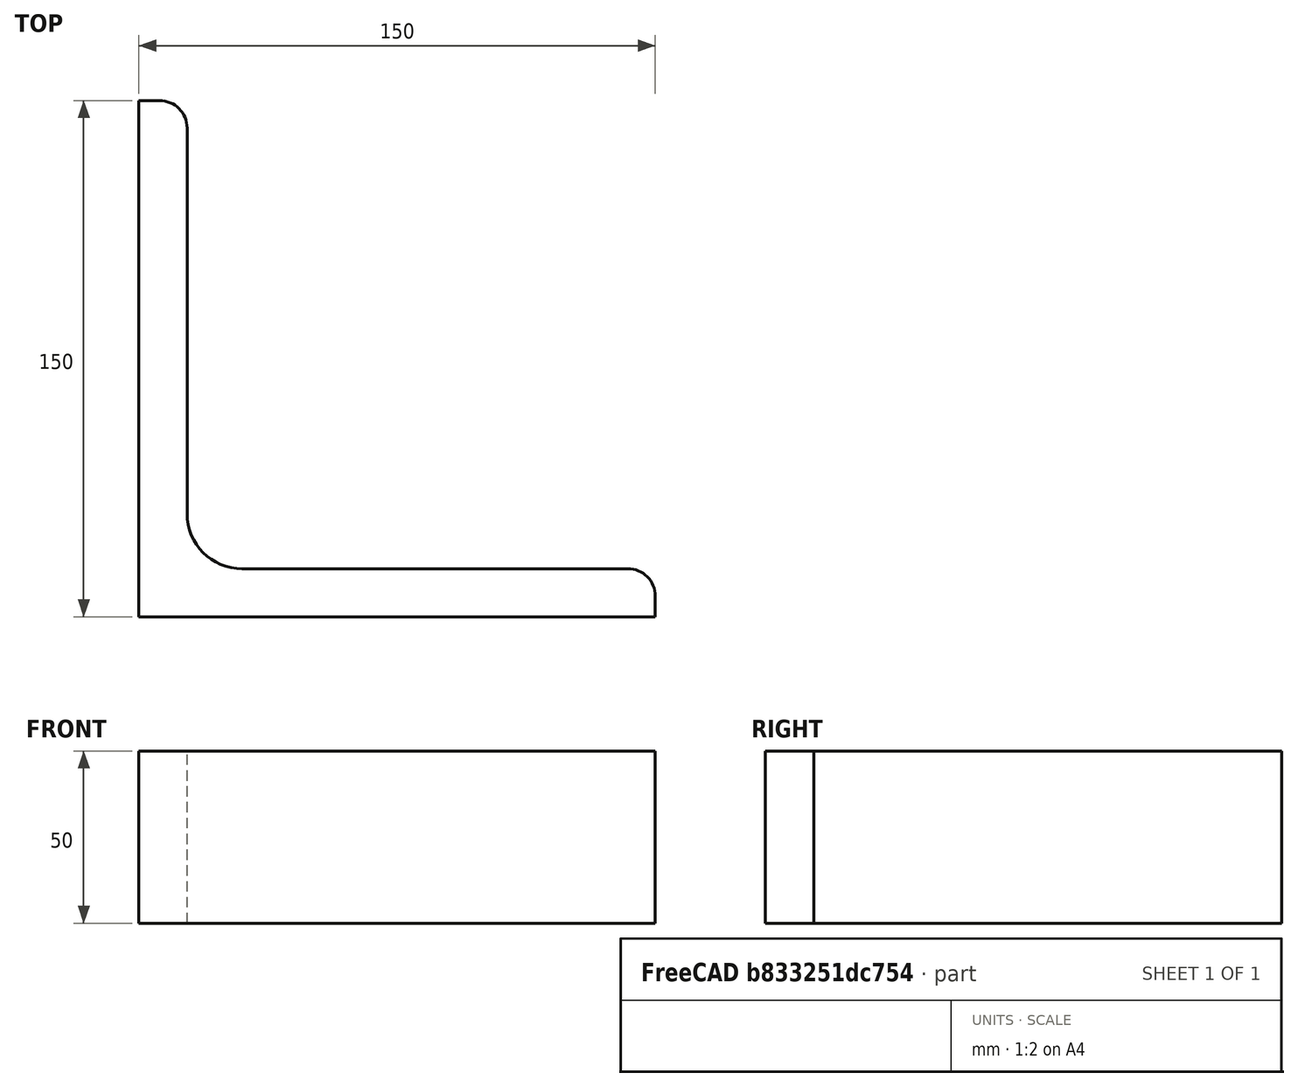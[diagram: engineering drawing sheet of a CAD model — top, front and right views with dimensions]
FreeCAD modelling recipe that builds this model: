
FCSTD DOCUMENT  (FreeCAD 0.15R4671 (Git))
Label: Angle Bar L150x150x14 EN10056 S235JR
License: All rights reserved
LicenseURL: http://en.wikipedia.org/wiki/All_rights_reserved
objects: Sketcher::SketchObject×1, Part::Extrusion×1
note: 2 computed .brp shape members not serialized (recipe doc carries the construction recipe); baked Part::Feature solids carry a one-line shape summary decoded from their .brp

FEATURE [Sketcher::SketchObject] Sketch
  sketch-geometry (9):
    g0: LineSegment StartX=0 StartY=0 StartZ=0 EndX=150 EndY=0 EndZ=0
    g1: LineSegment StartX=150 StartY=0 StartZ=0 EndX=150 EndY=6 EndZ=0
    g2: LineSegment StartX=142 StartY=14 StartZ=0 EndX=30 EndY=14 EndZ=0
    g3: LineSegment StartX=0 StartY=0 StartZ=0 EndX=0 EndY=150 EndZ=0
    g4: LineSegment StartX=0 StartY=150 StartZ=0 EndX=6 EndY=150 EndZ=0
    g5: LineSegment StartX=14 StartY=142 StartZ=0 EndX=14 EndY=30 EndZ=0
    g6: ArcOfCircle CenterX=30 CenterY=30 CenterZ=0 NormalX=0 NormalY=0 NormalZ=1 Radius=16 StartAngle=3.14159 EndAngle=4.71239
    g7: ArcOfCircle CenterX=6 CenterY=142 CenterZ=0 NormalX=0 NormalY=0 NormalZ=1 Radius=8 StartAngle=0 EndAngle=1.5708
    g8: ArcOfCircle CenterX=142 CenterY=6 CenterZ=0 NormalX=0 NormalY=0 NormalZ=1 Radius=8 StartAngle=0 EndAngle=1.5708
  constraints (23):
    c: Coincident(g0,g-1)
    c: Horizontal(g0)
    c: Coincident(g1,g0)
    c: Vertical(g1)
    c: Horizontal(g2)
    c: Coincident(g3,g-1)
    c: Vertical(g3)
    c: Coincident(g4,g3)
    c: Horizontal(g4)
    c: Vertical(g5)
    c: Tangent(g5,g6) = -1.5708
    c: Tangent(g2,g6) = 1.5708
    c: Tangent(g4,g7) = 1.5708
    c: Tangent(g5,g7) = 1.5708
    c: Tangent(g2,g8) = -1.5708
    c: Tangent(g1,g8) = -1.5708
    c: DistanceX(g0) = 150
    c: DistanceY(g3) = 150
    c: DistanceY(g0,g2) = 14
    c: DistanceX(g3,g5) = 14
    c: Radius(g6) = 16
    c: Radius(g8) = 8
    c: Radius(g7) = 8
FEATURE [Part::Extrusion] Extrude  label="Angle Bar L150x150x14 EN10056 S235JR"
  Base = -> Sketch
  Dir = (0,0,50)
  Solid = true
